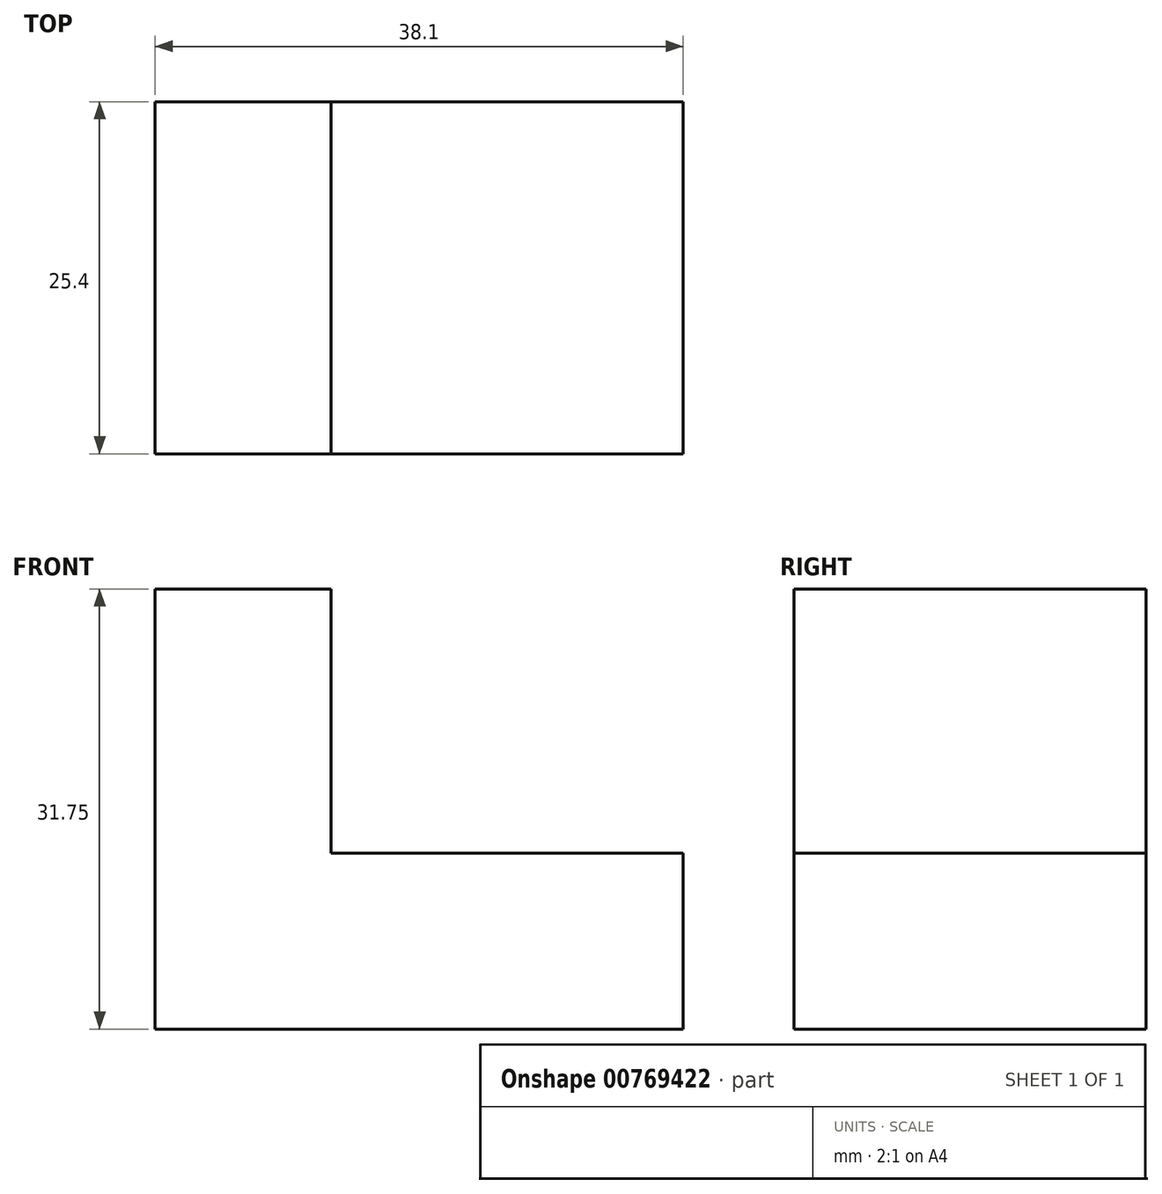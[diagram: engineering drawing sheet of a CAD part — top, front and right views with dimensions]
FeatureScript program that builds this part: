
annotation { "Feature Type Name" : "Feature", "Feature Type Description" : "" }
export const myFeature = defineFeature(function(context is Context, id is Id, definition is map)
    precondition{}
    {
        {
            var Q0;
            Q0=qCreatedBy(makeId("Front.planeOp"),FACE);
            var sketch = newSketch(context, id + "F0", { "sketchPlane" : qUnion([Q0])});
            skLineSegment(sketch, "E0", {"start": v(0, 0) * mm, "end": v(38.1, 0) * mm});
            skLineSegment(sketch, "E1", {"start": v(0, 0) * mm, "end": v(0, 31.75) * mm});
            skLineSegment(sketch, "E2", {"start": v(0, 31.75) * mm, "end": v(12.7, 31.75) * mm});
            skLineSegment(sketch, "E3", {"start": v(38.1, 0) * mm, "end": v(38.1, 12.7) * mm});
            skLineSegment(sketch, "E4", {"start": v(38.1, 12.7) * mm, "end": v(12.7, 12.7) * mm});
            skLineSegment(sketch, "E5", {"start": v(12.7, 12.7) * mm, "end": v(12.7, 31.75) * mm});
            skSolve(sketch);
        }
        {
            var Q0;
            Q0=makeQuery(id+"F0.imprint","IMPRINT",FACE,{"disambiguationData":[TD([[makeQuery(id+"F0.imprint","IMPRINT",EDGE,{"derivedFrom":sQuery(id+"F0.wireOp",EDGE,"E0")}),1.0]])]});
            var Q1;
            Q1=sQuery(id+"F0.wireOp",EDGE,"E4");
            var Q2;
            Q2=sQuery(id+"F0.wireOp",EDGE,"E5");
            var Q3;
            Q3=sQuery(id+"F0.wireOp",EDGE,"E2");
            var Q4;
            Q4=sQuery(id+"F0.wireOp",EDGE,"E1");
            var Q5;
            Q5=sQuery(id+"F0.wireOp",EDGE,"E3");
            var Q6;
            Q6=sQuery(id+"F0.wireOp",EDGE,"E0");
            extrude(context, id + "F1", {"entities" : qUnion([Q0]), "surfaceEntities" : qUnion([Q1, Q2, Q3, Q4, Q5, Q6]), "endBound" : BoundingType.SYMMETRIC, "oppositeDirection" : true, "depth" : 25.4 * mm, "offsetDistance" : 25.4 * mm});
        }
    });
